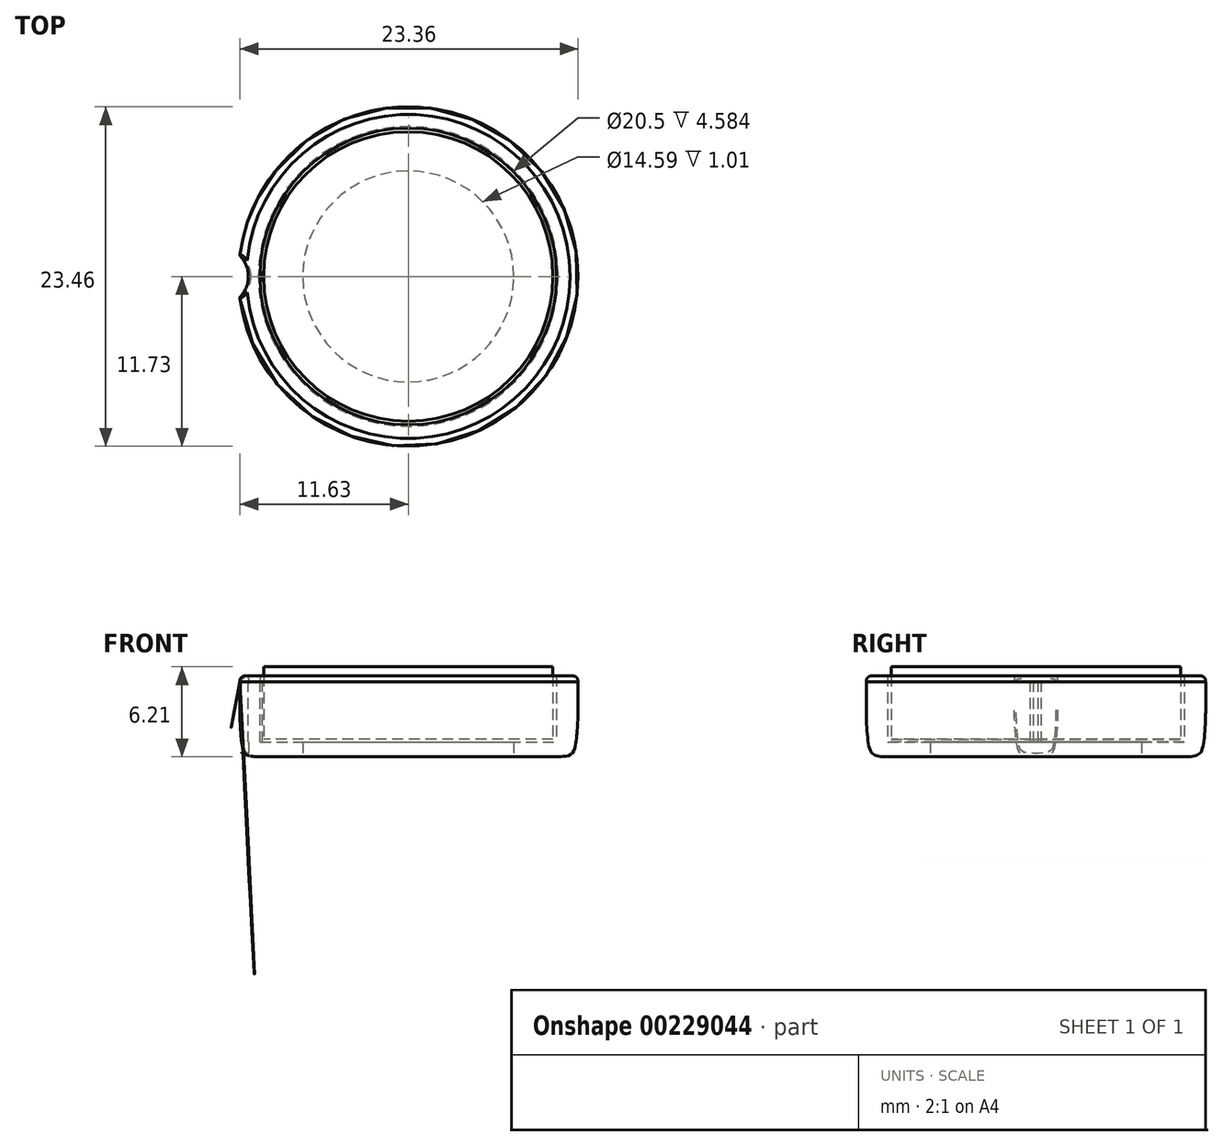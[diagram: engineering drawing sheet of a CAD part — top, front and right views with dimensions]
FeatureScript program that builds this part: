
annotation { "Feature Type Name" : "Feature", "Feature Type Description" : "" }
export const myFeature = defineFeature(function(context is Context, id is Id, definition is map)
    precondition{}
    {
        {
            var Q0;
            Q0=qCreatedBy(makeId("Top.planeOp"),FACE);
            var sketch = newSketch(context, id + "F0", { "sketchPlane" : qUnion([Q0])});
            skCircle(sketch, "E0", {"center": v(0, 0) * mm, "radius": 10 * mm});
            skSolve(sketch);
        }
        {
            var Q0;
            Q0=makeQuery(id+"F0.imprint","IMPRINT",FACE,{"disambiguationData":[TD([[makeQuery(id+"F0.imprint","IMPRINT",EDGE,{"derivedFrom":sQuery(id+"F0.wireOp",EDGE,"E0")}),1.0]])]});
            extrude(context, id + "F1", {"entities" : qUnion([Q0]), "depth" : 5 * mm});
        }
        {
            var Q0;
            Q0=qCreatedBy(makeId("Front.planeOp"),FACE);
            var sketch = newSketch(context, id + "F2", { "sketchPlane" : qUnion([Q0])});
            skLineSegment(sketch, "E1", {"start": v(-10, 6.11) * mm, "end": v(-10, -0.2) * mm, "construction": true});
            skLineSegment(sketch, "E2", {"start": v(-10.25, 4.38) * mm, "end": v(-10.25, -0.2) * mm, "construction": true});
            skLineSegment(sketch, "E3", {"start": v(0, 0) * mm, "end": v(-10, 0) * mm});
            skLineSegment(sketch, "E4", {"start": v(-7.3, -0.2) * mm, "end": v(-11.78, -0.2) * mm, "construction": true});
            skLineSegment(sketch, "E5.bottom", {"start": v(-11.2, 4.38) * mm, "end": v(-10.25, 4.38) * mm});
            skLineSegment(sketch, "E5.left", {"start": v(-10.25, 4.38) * mm, "end": v(-10.25, -0.29) * mm});
            skLineSegment(sketch, "E6.top", {"start": v(-10.25, -0.2) * mm, "end": v(-7.3, -0.2) * mm});
            skLineSegment(sketch, "E7", {"start": v(-10.36, -1.21) * mm, "end": v(-7.3, -1.21) * mm});
            skPoint(sketch, "E8.visualSharp", {"position": v(-11.03, 4.38) * mm});
            skFitSpline(sketch, "E9", {"points": [v(-11.2, 4.38) * mm, v(-11.78, 3.12) * mm, v(-14.1, 0.05) * mm], "startDerivative": vector(-6.08, -0.07) * mm, "endDerivative": vector(-2.9, 5.2) * mm});
            skLineSegment(sketch, "E10", {"start": v(-7.3, -0.2) * mm, "end": v(-7.3, -1.21) * mm});
            skLineSegment(sketch, "E11", {"start": v(-11.73, 3.97) * mm, "end": v(-11.73, 2) * mm});
            skFitSpline(sketch, "E12", {"points": [v(-11.73, 2) * mm, v(-11.53, -0.55) * mm, v(-10.36, -1.21) * mm], "startDerivative": vector(-0.01, -1.39) * mm, "endDerivative": vector(5.88, -0.09) * mm});
            skLineSegment(sketch, "E13", {"start": v(0, -1.1) * mm, "end": v(0, 6.97) * mm, "construction": true});
            skSolve(sketch);
        }
        {
            var Q0;
            {var subQ2=sQuery(id+"F2.wireOp",EDGE,"E5.bottom");Q0=makeQuery(id+"F2.imprint","IMPRINT",FACE,{"disambiguationData":[TD([[makeQuery(id+"F2.imprint","IMPRINT",EDGE,{"derivedFrom":subQ2}),-1.0]])]});}
            var Q1;
            Q1=sQuery(id+"F2.wireOp",EDGE,"E13");
            revolve(context, id + "F3", {"entities" : qUnion([Q0]), "axis" : qUnion([Q1]), "revolveType" : RevolveType.FULL});
        }
        {
            var Q0;
            Q0=makeQuery(id+"F3.opRevolve","SWEPT_FACE",FACE,{"disambiguationData":[OSD([sQuery(id+"F2.wireOp",EDGE,"E7")])]});
            cPlane(context, id + "F4", {"entities" : qUnion([Q0]), "cplaneType" : CPlaneType.OFFSET, "offset" : 2 * mm, "width" : 150 * mm, "height" : 150 * mm});
        }
        {
            var Q0;
            Q0=qCreatedBy(id+"F4.planeOp",FACE);
            var sketch = newSketch(context, id + "F5", { "sketchPlane" : qUnion([Q0])});
            skCircle(sketch, "E14", {"center": v(-13.05, 0) * mm, "radius": 2 * mm});
            skSolve(sketch);
        }
        {
            var Q0;
            Q0=makeQuery(id+"F5.imprint","IMPRINT",FACE,{"disambiguationData":[TD([[makeQuery(id+"F5.imprint","IMPRINT",EDGE,{"derivedFrom":sQuery(id+"F5.wireOp",EDGE,"E14")}),1.0]])]});
            var Q1;
            Q1=makeQuery(id+"F3.opRevolve","SWEPT_FACE",FACE,{"disambiguationData":[OSD([sQuery(id+"F2.wireOp",EDGE,"E5.bottom")])]});
            var Q2;
            Q2=makeQuery(id+"F3.opRevolve","SWEPT_BODY",BODY,{"disambiguationData":[OSD([sQuery(id+"F2.wireOp",EDGE,"E5.bottom"),sQuery(id+"F2.wireOp",EDGE,"E5.left"),sQuery(id+"F2.wireOp",EDGE,"E6.top"),sQuery(id+"F2.wireOp",EDGE,"E7"),sQuery(id+"F2.wireOp",EDGE,"E9"),sQuery(id+"F2.wireOp",EDGE,"E10"),sQuery(id+"F2.wireOp",EDGE,"E11"),sQuery(id+"F2.wireOp",EDGE,"E12")])]});
            extrude(context, id + "F6", {"entities" : qUnion([Q0]), "operationType" : NewBodyOperationType.REMOVE, "endBound" : BoundingType.THROUGH_ALL, "oppositeDirection" : true, "endBoundEntityFace" : qUnion([Q1]), "endBoundEntityBody" : qUnion([Q2]), "depth" : 25 * mm});
        }
        {
            var Q0;
            Q0=makeQuery(id+"F6.boolean.opBoolean","INTERSECT",EDGE,{"derivedFrom":[makeQuery(id+"F3.opRevolve","SWEPT_FACE",FACE,{"disambiguationData":[OSD([sQuery(id+"F2.wireOp",EDGE,"E9")])]}),makeQuery(id+"F6.opExtrude","SWEPT_FACE",FACE,{"disambiguationData":[OSD([sQuery(id+"F5.wireOp",EDGE,"E14")])]})]});
            var Q1;
            Q1=makeQuery(id+"F6.boolean.opBoolean","INTERSECT",EDGE,{"disambiguationData":[OD(1.0)],"derivedFrom":[makeQuery(id+"F3.opRevolve","SWEPT_FACE",FACE,{"disambiguationData":[OSD([sQuery(id+"F2.wireOp",EDGE,"E11")])]}),makeQuery(id+"F6.opExtrude","SWEPT_FACE",FACE,{"disambiguationData":[OSD([sQuery(id+"F5.wireOp",EDGE,"E14")])]})]});
            var Q2;
            Q2=makeQuery(id+"F6.boolean.opBoolean","INTERSECT",EDGE,{"disambiguationData":[OD(1.0)],"derivedFrom":[makeQuery(id+"F3.opRevolve","SWEPT_FACE",FACE,{"disambiguationData":[OSD([sQuery(id+"F2.wireOp",EDGE,"E12")])]}),makeQuery(id+"F6.opExtrude","SWEPT_FACE",FACE,{"disambiguationData":[OSD([sQuery(id+"F5.wireOp",EDGE,"E14")])]})]});
            var Q3;
            Q3=makeQuery(id+"F6.boolean.opBoolean","INTERSECT",EDGE,{"derivedFrom":[makeQuery(id+"F3.opRevolve","SWEPT_FACE",FACE,{"disambiguationData":[OSD([sQuery(id+"F2.wireOp",EDGE,"E7")])]}),makeQuery(id+"F6.opExtrude","SWEPT_FACE",FACE,{"disambiguationData":[OSD([sQuery(id+"F5.wireOp",EDGE,"E14")])]})]});
            var Q4;
            Q4=makeQuery(id+"F6.boolean.opBoolean","INTERSECT",EDGE,{"disambiguationData":[OD(0.0)],"derivedFrom":[makeQuery(id+"F3.opRevolve","SWEPT_FACE",FACE,{"disambiguationData":[OSD([sQuery(id+"F2.wireOp",EDGE,"E12")])]}),makeQuery(id+"F6.opExtrude","SWEPT_FACE",FACE,{"disambiguationData":[OSD([sQuery(id+"F5.wireOp",EDGE,"E14")])]})]});
            var Q5;
            Q5=makeQuery(id+"F6.boolean.opBoolean","INTERSECT",EDGE,{"disambiguationData":[OD(0.0)],"derivedFrom":[makeQuery(id+"F3.opRevolve","SWEPT_FACE",FACE,{"disambiguationData":[OSD([sQuery(id+"F2.wireOp",EDGE,"E11")])]}),makeQuery(id+"F6.opExtrude","SWEPT_FACE",FACE,{"disambiguationData":[OSD([sQuery(id+"F5.wireOp",EDGE,"E14")])]})]});
            fillet(context, id + "F7", {"entities" : qUnion([Q0, Q1, Q2, Q3, Q4, Q5]), "radius" : .2 * mm, "allowEdgeOverflow" : false});
        }
        {
            var Q0;
            Q0=makeQuery(id+"F1.opExtrude","CAP_FACE",FACE,{"disambiguationData":[OSD([sQuery(id+"F0.wireOp",EDGE,"E0")])],"isStart":false});
            cPlane(context, id + "F8", {"entities" : qUnion([Q0]), "cplaneType" : CPlaneType.OFFSET, "offset" : 1 * mm, "oppositeDirection" : true, "width" : 150 * mm, "height" : 150 * mm});
        }
        {
            var Q0;
            Q0=qCreatedBy(id+"F8.planeOp",FACE);
            var sketch = newSketch(context, id + "F9", { "sketchPlane" : qUnion([Q0])});
            skCircle(sketch, "E15", {"center": v(-10.58, 0) * mm, "radius": 0.5 * mm});
            skCircle(sketch, "E16", {"center": v(0, 0) * mm, "radius": 10 * mm, "construction": true});
            skSolve(sketch);
        }
        {
            var Q0;
            Q0 = qSketchRegion(id + "F9", true);
            var Q1;
            Q1 = qConstructionFilter(qBodyType(qCreatedBy(id + "F9" ,EDGE), BodyType.WIRE), ConstructionObject.NO);
            var Q2;
            Q2=makeQuery(id+"F3.opRevolve","SWEPT_FACE",FACE,{"disambiguationData":[OSD([sQuery(id+"F2.wireOp",EDGE,"E6.top")])]});
            extrude(context, id + "F10", {"entities" : qUnion([Q0]), "operationType" : NewBodyOperationType.ADD, "surfaceEntities" : qUnion([Q1]), "endBound" : BoundingType.UP_TO_SURFACE, "oppositeDirection" : true, "endBoundEntityFace" : qUnion([Q2]), "depth" : 5 * mm});
        }
        {
            var Q0;
            Q0=makeQuery(id+"F10.opExtrude","CAP_EDGE",EDGE,{"disambiguationData":[OSD([sQuery(id+"F9.wireOp",EDGE,"E15")])],"isStart":true});
            var Q1;
            {var subQ0=sQuery(id+"F9.wireOp",EDGE,"E15");var subQ1=sQuery(id+"F2.wireOp",EDGE,"E6.top");Q1=makeQuery(id+"F10.boolean.opBoolean","SPLIT",EDGE,{"disambiguationData":[TD([makeQuery(id+"F6.boolean.opBoolean","COPY",FACE,{"derivedFrom":makeQuery(id+"F6.opExtrude","SWEPT_FACE",FACE,{"disambiguationData":[OSD([sQuery(id+"F5.wireOp",EDGE,"E14")])]})})])],"derivedFrom":makeQuery(id+"F10.opExtrude","TWEAK_EDGE",EDGE,{"derivedFrom":[makeQuery(id+"F3.opRevolve","SWEPT_FACE",FACE,{"disambiguationData":[OSD([subQ1])]}),makeQuery(id+"F9.imprint","IMPRINT",EDGE,{"derivedFrom":subQ0})]})});}
            fillet(context, id + "F11", {"entities" : qUnion([Q0, Q1]), "radius" : .2 * mm, "tangentPropagation" : true, "allowEdgeOverflow" : false});
        }
    });
